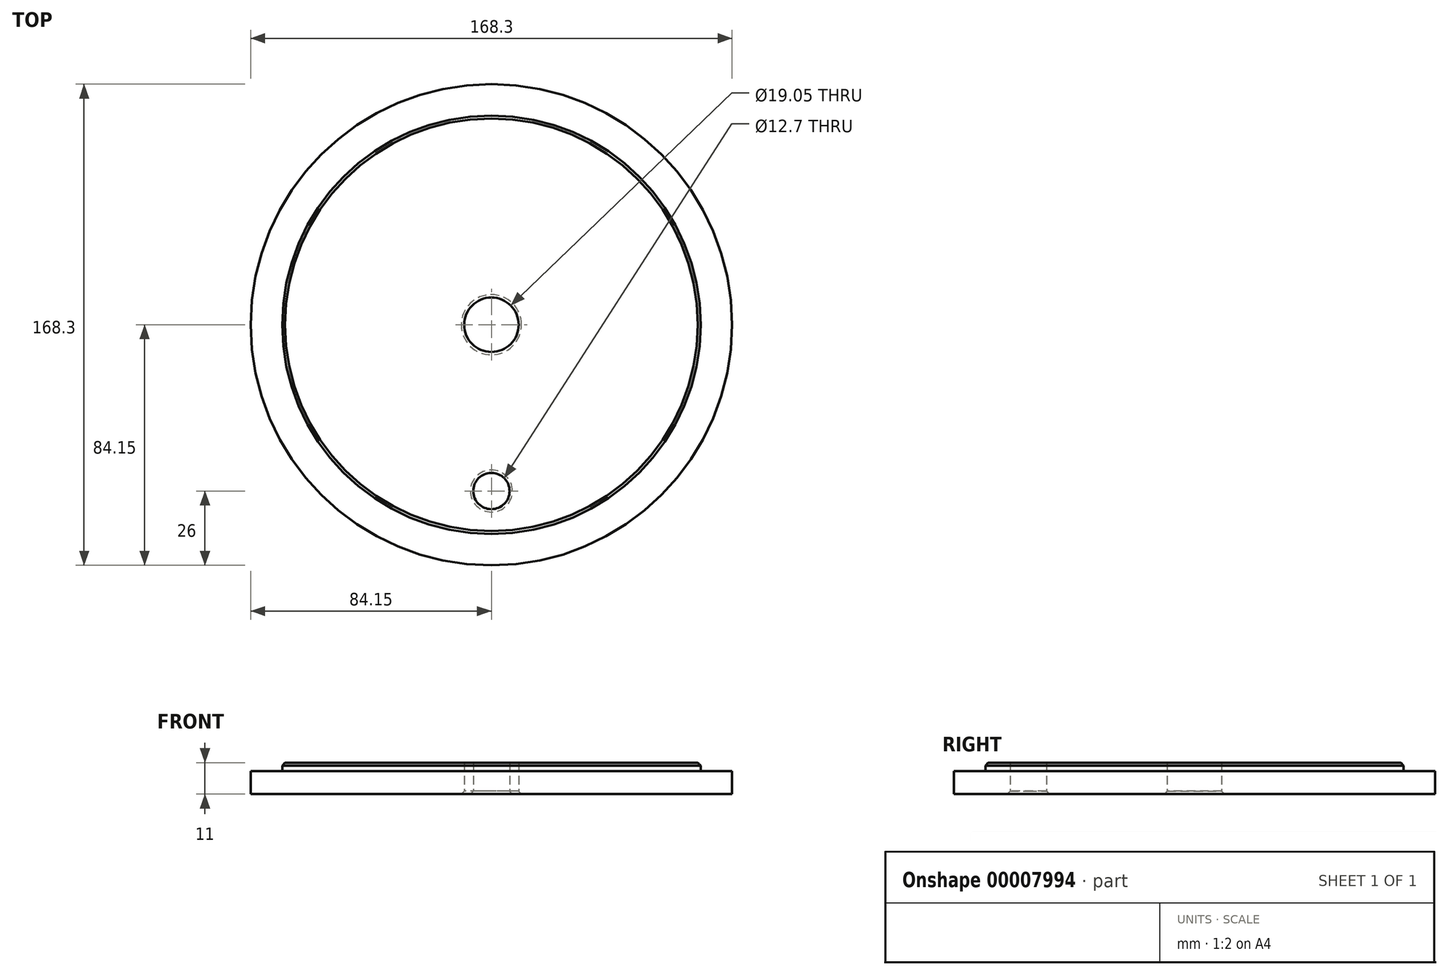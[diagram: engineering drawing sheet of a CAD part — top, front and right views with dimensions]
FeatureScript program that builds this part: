
annotation { "Feature Type Name" : "Feature", "Feature Type Description" : "" }
export const myFeature = defineFeature(function(context is Context, id is Id, definition is map)
    precondition{}
    {
        {
            var Q0;
            Q0=qCreatedBy(makeId("Top.planeOp"),FACE);
            var sketch = newSketch(context, id + "F0", { "sketchPlane" : qUnion([Q0])});
            skCircle(sketch, "E0", {"center": v(0, 0) * mm, "radius": 84.15 * mm});
            skCircle(sketch, "E1", {"center": v(0, 0) * mm, "radius": 73.15 * mm});
            skCircle(sketch, "E2", {"center": v(0, 0) * mm, "radius": 9.52 * mm});
            skCircle(sketch, "E3", {"center": v(0, -58.15) * mm, "radius": 6.35 * mm});
            skSolve(sketch);
        }
        {
            var Q0;
            Q0=makeQuery(id+"F0.imprint","IMPRINT",FACE,{"disambiguationData":[TD([[makeQuery(id+"F0.imprint","IMPRINT",EDGE,{"derivedFrom":sQuery(id+"F0.wireOp",EDGE,"E1")}),1.0]])]});
            extrude(context, id + "F1", {"entities" : qUnion([Q0]), "depth" : 11 * mm});
        }
        {
            var Q0;
            Q0 = qSketchRegion(id + "F0", true);
            extrude(context, id + "F2", {"entities" : qUnion([Q0]), "operationType" : NewBodyOperationType.ADD, "depth" : 8 * mm});
        }
        {
            var Q0;
            Q0=makeQuery(id+"F1.opExtrude","CAP_EDGE",EDGE,{"disambiguationData":[OSD([sQuery(id+"F0.wireOp",EDGE,"E1")])],"isStart":false});
            var Q1;
            Q1=makeQuery(id+"F1.opExtrude","CAP_EDGE",EDGE,{"disambiguationData":[OSD([sQuery(id+"F0.wireOp",EDGE,"E2")])],"isStart":true});
            var Q2;
            Q2=makeQuery(id+"F1.opExtrude","CAP_EDGE",EDGE,{"disambiguationData":[OSD([sQuery(id+"F0.wireOp",EDGE,"E3")])],"isStart":true});
            chamfer(context, id + "F3", {"entities" : qUnion([Q0, Q1, Q2]), "width" : 1 * mm, "tangentPropagation" : true});
        }
    });
